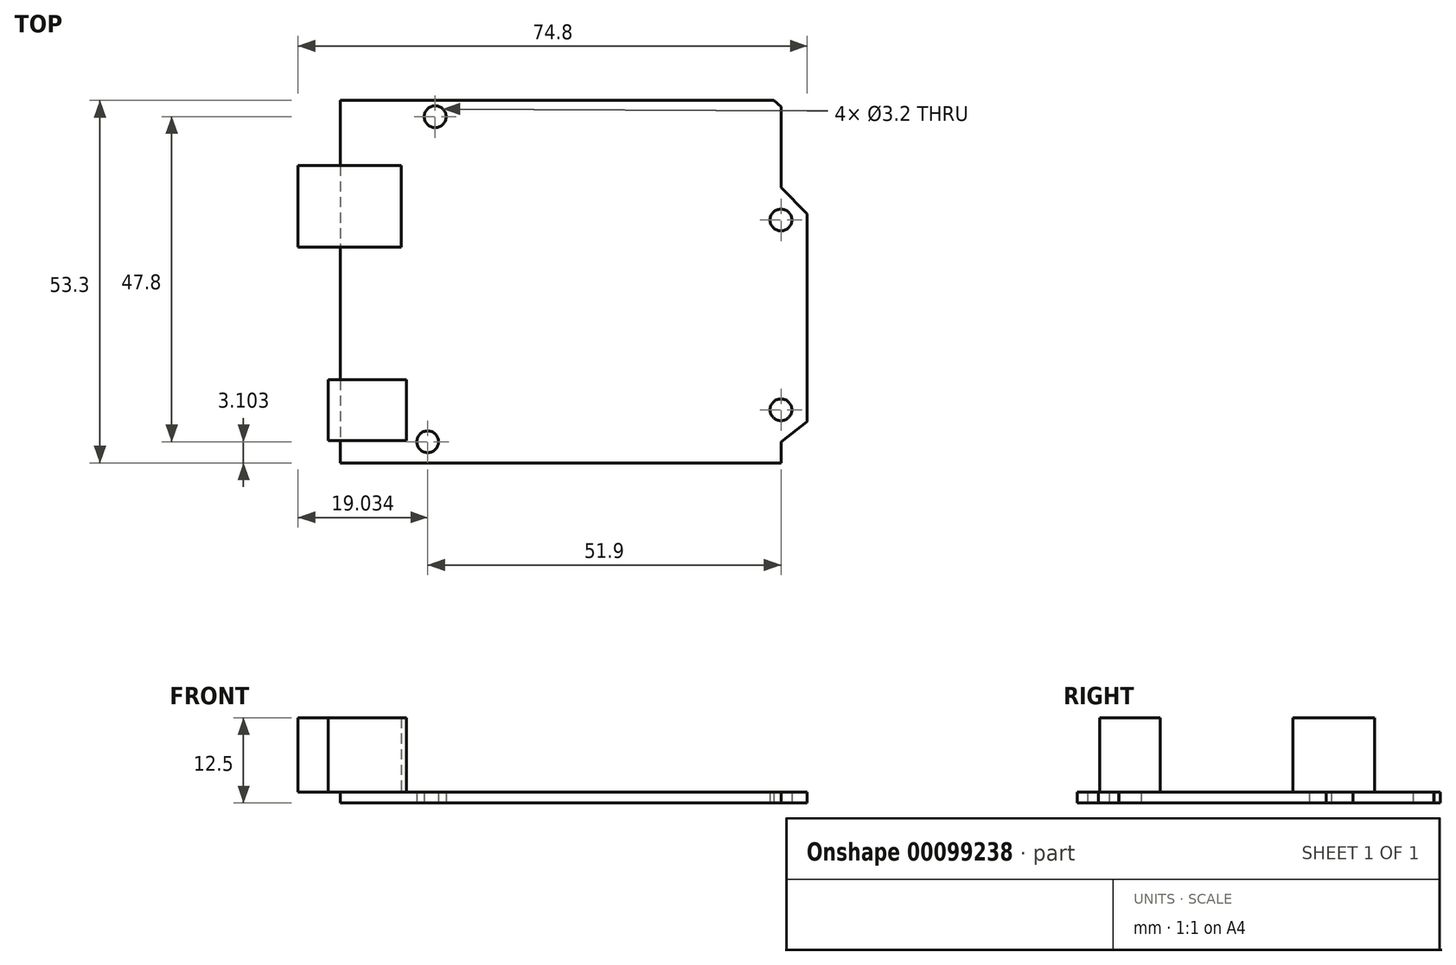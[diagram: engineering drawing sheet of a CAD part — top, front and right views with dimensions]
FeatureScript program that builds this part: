
annotation { "Feature Type Name" : "Feature", "Feature Type Description" : "" }
export const myFeature = defineFeature(function(context is Context, id is Id, definition is map)
    precondition{}
    {
        {
            var Q0;
            Q0=qCreatedBy(makeId("Top.planeOp"),FACE);
            var sketch = newSketch(context, id + "F0", { "sketchPlane" : qUnion([Q0])});
            skLineSegment(sketch, "E0.bottom", {"start": v(-34.55, 26.84) * mm, "end": v(29.16, 26.84) * mm});
            skLineSegment(sketch, "E0.top", {"start": v(-34.55, -26.46) * mm, "end": v(30.18, -26.46) * mm});
            skLineSegment(sketch, "E0.left", {"start": v(-34.55, 26.84) * mm, "end": v(-34.55, -26.46) * mm});
            skLineSegment(sketch, "E0.right", {"start": v(34.05, 10.12) * mm, "end": v(34.05, -20.37) * mm});
            skCircle(sketch, "E1", {"center": v(-20.62, 24.44) * mm, "radius": 1.6 * mm});
            skCircle(sketch, "E2", {"center": v(30.18, -18.66) * mm, "radius": 1.6 * mm});
            skCircle(sketch, "E3", {"center": v(30.18, 9.24) * mm, "radius": 1.6 * mm});
            skLineSegment(sketch, "E4", {"start": v(34.05, 10.12) * mm, "end": v(30.18, 14.02) * mm});
            skLineSegment(sketch, "E5", {"start": v(30.18, 14.02) * mm, "end": v(30.18, 25.89) * mm});
            skLineSegment(sketch, "E6", {"start": v(30.18, 25.89) * mm, "end": v(29.16, 26.84) * mm});
            skLineSegment(sketch, "E7", {"start": v(30.18, -26.46) * mm, "end": v(30.18, -23.36) * mm});
            skLineSegment(sketch, "E8", {"start": v(30.18, -23.36) * mm, "end": v(34.05, -20.37) * mm});
            skCircle(sketch, "E9", {"center": v(-21.72, -23.36) * mm, "radius": 1.6 * mm});
            skSolve(sketch);
        }
        {
            var Q0;
            Q0=makeQuery(id+"F0.imprint","IMPRINT",FACE,{"disambiguationData":[TD([[makeQuery(id+"F0.imprint","IMPRINT",EDGE,{"derivedFrom":sQuery(id+"F0.wireOp",EDGE,"E0.bottom")}),-1.0]])]});
            extrude(context, id + "F1", {"entities" : qUnion([Q0]), "depth" : 1.6 * mm});
        }
        {
            var Q0;
            Q0=makeQuery(id+"F1.opExtrude","CAP_FACE",FACE,{"disambiguationData":[OSD([sQuery(id+"F0.wireOp",EDGE,"E0.bottom"),sQuery(id+"F0.wireOp",EDGE,"E0.top"),sQuery(id+"F0.wireOp",EDGE,"E0.left"),sQuery(id+"F0.wireOp",EDGE,"E0.right"),sQuery(id+"F0.wireOp",EDGE,"E1"),sQuery(id+"F0.wireOp",EDGE,"E2"),sQuery(id+"F0.wireOp",EDGE,"E3"),sQuery(id+"F0.wireOp",EDGE,"E4"),sQuery(id+"F0.wireOp",EDGE,"E5"),sQuery(id+"F0.wireOp",EDGE,"E6"),sQuery(id+"F0.wireOp",EDGE,"E7"),sQuery(id+"F0.wireOp",EDGE,"E8"),sQuery(id+"F0.wireOp",EDGE,"E9")])],"isStart":false});
            var sketch = newSketch(context, id + "F2", { "sketchPlane" : qUnion([Q0])});
            skLineSegment(sketch, "E10.bottom", {"start": v(-40.75, 17.24) * mm, "end": v(-25.63, 17.24) * mm});
            skLineSegment(sketch, "E10.top", {"start": v(-40.75, 5.24) * mm, "end": v(-25.63, 5.24) * mm});
            skLineSegment(sketch, "E10.left", {"start": v(-40.75, 17.24) * mm, "end": v(-40.75, 5.24) * mm});
            skLineSegment(sketch, "E10.right", {"start": v(-25.63, 17.24) * mm, "end": v(-25.63, 5.24) * mm});
            skLineSegment(sketch, "E11.bottom", {"start": v(-36.35, -14.26) * mm, "end": v(-24.83, -14.26) * mm});
            skLineSegment(sketch, "E11.top", {"start": v(-36.35, -23.16) * mm, "end": v(-24.83, -23.16) * mm});
            skLineSegment(sketch, "E11.left", {"start": v(-36.35, -14.26) * mm, "end": v(-36.35, -23.16) * mm});
            skLineSegment(sketch, "E11.right", {"start": v(-24.83, -14.26) * mm, "end": v(-24.83, -23.16) * mm});
            skSolve(sketch);
        }
        {
            var Q0;
            Q0=makeQuery(id+"F2.imprint","IMPRINT",FACE,{"disambiguationData":[TD([[makeQuery(id+"F2.imprint","IMPRINT",EDGE,{"derivedFrom":sQuery(id+"F2.wireOp",EDGE,"E10.bottom")}),-1.0]])]});
            var Q1;
            Q1=makeQuery(id+"F2.imprint","IMPRINT",FACE,{"disambiguationData":[TD([[makeQuery(id+"F2.imprint","IMPRINT",EDGE,{"derivedFrom":sQuery(id+"F2.wireOp",EDGE,"E11.bottom")}),-1.0]])]});
            extrude(context, id + "F3", {"entities" : qUnion([Q0, Q1]), "operationType" : NewBodyOperationType.ADD, "depth" : 10.9 * mm});
        }
    });
